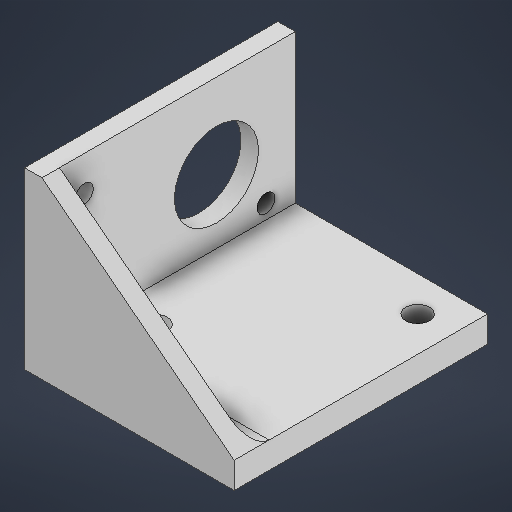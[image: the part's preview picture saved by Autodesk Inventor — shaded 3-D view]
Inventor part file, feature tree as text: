
AUTODESK INVENTOR PART (.ipt)
format: ipt  version: 2025.4 (Build 294407000, 407)  size: 414,208 bytes
history: native  units: in
note: dims shown in document units (in); Inventor stores cm internally (conversion verified against a paired STEP export)
features: extrude x4, sketch x4, fillet x1, projected_geometry x1
ambient origin geometry x8: Origin, YZ Plane, XZ Plane, XY Plane, X Axis, Y Axis, Z Axis, Center Point
bodies: Solid1 (feature_tree)
feature tree (10):
  extrude  "Extrusion1"  Depth=1.25in
  extrude  "Extrusion2"  Depth=0.1875in
  extrude  "Extrusion3"  Depth=1.8125in
  extrude  "Extrusion4"  Depth=0.125in
  fillet  "Fillet1"  Radius=1.2992in
  sketch  "Sketch1"  dims[d1=0.125in d2=1.25in]
  sketch  "Sketch2"  dims[d3=1.5in d4=0.1875in]
  sketch  "Sketch3"  dims[d5=1.8125in d6=0.0in d24=0.128in]
  projected_geometry  "Projected Loop1"
  sketch  "Sketch4"  dims[d25=0.128in d26=0.128in d27=1.2992in d35=1.8125in d36=0.0in d38=0.6in d39=0.125in d40=0.0in d41=0.17in d42=0.17in d43=0.25in d44=0.25in d45=0.4375in d47=0.25in d48=0.125in d49=0.0in d50=0.3438in d51=0.125in d53=0.25in d54=0.3543in d55=0.7087in d56=0.21in d57=0.3543in]
